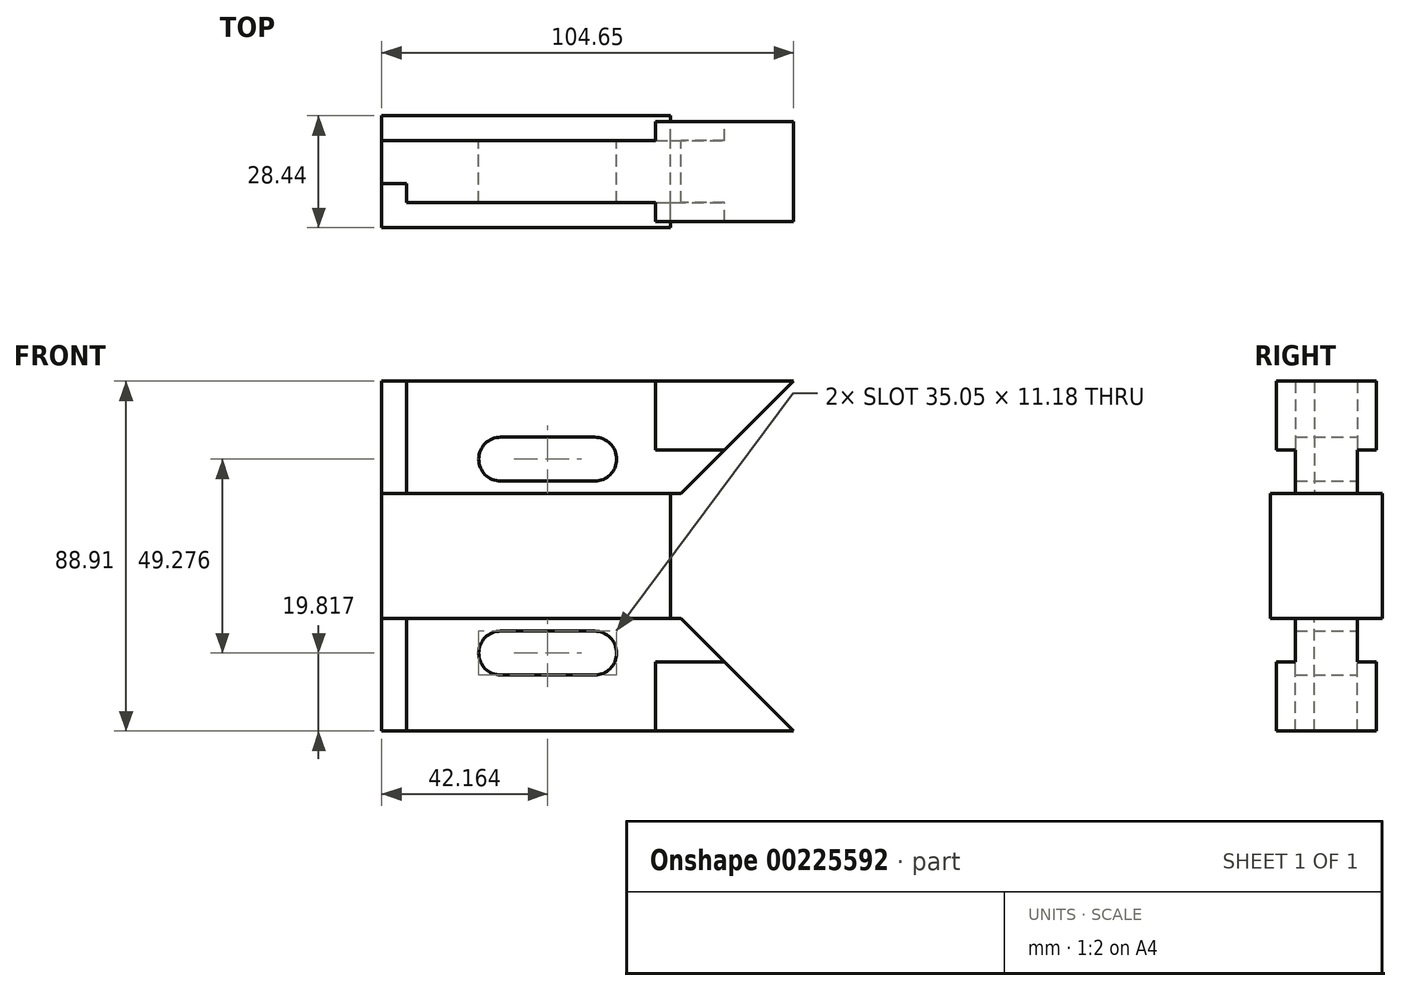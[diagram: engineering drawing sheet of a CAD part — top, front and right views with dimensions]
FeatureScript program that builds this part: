
annotation { "Feature Type Name" : "Feature", "Feature Type Description" : "" }
export const myFeature = defineFeature(function(context is Context, id is Id, definition is map)
    precondition{}
    {
        {
            var Q0;
            Q0=qCreatedBy(makeId("Front.planeOp"),FACE);
            var sketch = newSketch(context, id + "F0", { "sketchPlane" : qUnion([Q0])});
            skLineSegment(sketch, "E0", {"start": v(0, 28.57) * mm, "end": v(0, 0) * mm});
            skLineSegment(sketch, "E1", {"start": v(0, 0) * mm, "end": v(104.65, 0) * mm});
            skLineSegment(sketch, "E2", {"start": v(104.65, 0) * mm, "end": v(104.65, 28.57) * mm});
            skLineSegment(sketch, "E3", {"start": v(104.65, 28.58) * mm, "end": v(0, 28.57) * mm});
            skLineSegment(sketch, "E4", {"start": v(0, 0) * mm, "end": v(0, -15.87) * mm});
            skLineSegment(sketch, "E5", {"start": v(0, -15.88) * mm, "end": v(73.4, -15.88) * mm});
            skLineSegment(sketch, "E6", {"start": v(73.4, -15.88) * mm, "end": v(73.4, 0) * mm});
            skLineSegment(sketch, "E7", {"start": v(104.65, 28.58) * mm, "end": v(76.07, 0) * mm});
            skLineSegment(sketch, "E8", {"start": v(69.6, 28.58) * mm, "end": v(69.6, 11.05) * mm});
            skLineSegment(sketch, "E9", {"start": v(69.6, 11.05) * mm, "end": v(104.65, 11.05) * mm});
            skLineSegment(sketch, "E10", {"start": v(6.35, 28.57) * mm, "end": v(6.35, 0) * mm});
            skCircle(sketch, "E11", {"center": v(30.23, 8.76) * mm, "radius": 5.59 * mm});
            skCircle(sketch, "E12", {"center": v(54.1, 8.76) * mm, "radius": 5.59 * mm});
            skLineSegment(sketch, "E13", {"start": v(30.23, 3.17) * mm, "end": v(30.23, 14.35) * mm});
            skLineSegment(sketch, "E14", {"start": v(30.23, 14.35) * mm, "end": v(54.1, 14.35) * mm});
            skLineSegment(sketch, "E15", {"start": v(54.1, 14.35) * mm, "end": v(54.1, 3.17) * mm});
            skLineSegment(sketch, "E16", {"start": v(54.1, 3.17) * mm, "end": v(30.23, 3.17) * mm});
            skSolve(sketch);
        }
        {
            var Q0;
            {var subQ0=sQuery(id+"F0.wireOp",EDGE,"E4");Q0=makeQuery(id+"F0.imprint","IMPRINT",FACE,{"disambiguationData":[TD([[makeQuery(id+"F0.imprint","IMPRINT",EDGE,{"derivedFrom":subQ0}),1.0]])]});}
            extrude(context, id + "F1", {"entities" : qUnion([Q0]), "endBound" : BoundingType.SYMMETRIC, "depth" : 28.45 * mm});
        }
        {
            var Q0;
            {var subQ3=sQuery(id+"F0.wireOp",EDGE,"E8");Q0=makeQuery(id+"F0.imprint","IMPRINT",FACE,{"disambiguationData":[TD([[makeQuery(id+"F0.imprint","IMPRINT",EDGE,{"derivedFrom":subQ3}),1.0]])]});}
            extrude(context, id + "F2", {"entities" : qUnion([Q0]), "endBound" : BoundingType.SYMMETRIC, "depth" : 25.4 * mm});
        }
        {
            var Q0;
            {var subQ9=sQuery(id+"F0.wireOp",EDGE,"E8");Q0=makeQuery(id+"F0.imprint","IMPRINT",FACE,{"disambiguationData":[TD([[makeQuery(id+"F0.imprint","IMPRINT",EDGE,{"derivedFrom":subQ9}),-1.0]])]});}
            extrude(context, id + "F3", {"entities" : qUnion([Q0]), "endBound" : BoundingType.SYMMETRIC, "depth" : 15.75 * mm});
        }
        {
            var Q0;
            {var subQ0=sQuery(id+"F0.wireOp",EDGE,"E0");Q0=makeQuery(id+"F0.imprint","IMPRINT",FACE,{"disambiguationData":[TD([[makeQuery(id+"F0.imprint","IMPRINT",EDGE,{"derivedFrom":subQ0}),1.0]])]});}
            extrude(context, id + "F4", {"entities" : qUnion([Q0]), "oppositeDirection" : true, "depth" : 7.87 * mm});
        }
        {
            var Q0;
            {var subQ0=sQuery(id+"F0.wireOp",EDGE,"E0");Q0=makeQuery(id+"F0.imprint","IMPRINT",FACE,{"disambiguationData":[TD([[makeQuery(id+"F0.imprint","IMPRINT",EDGE,{"derivedFrom":subQ0}),1.0]])]});}
            extrude(context, id + "F5", {"entities" : qUnion([Q0]), "depth" : 3.05 * mm});
        }
        {
            var Q0;
            Q0=makeQuery(id+"F1.opExtrude","SWEPT_BODY",BODY,{"disambiguationData":[OSD([sQuery(id+"F0.wireOp",EDGE,"E1"),sQuery(id+"F0.wireOp",EDGE,"E4"),sQuery(id+"F0.wireOp",EDGE,"E5"),sQuery(id+"F0.wireOp",EDGE,"E6")])]});
            var Q1;
            Q1=makeQuery(id+"F5.opExtrude","SWEPT_BODY",BODY,{"disambiguationData":[OSD([sQuery(id+"F0.wireOp",EDGE,"E0"),sQuery(id+"F0.wireOp",EDGE,"E1"),sQuery(id+"F0.wireOp",EDGE,"E3"),sQuery(id+"F0.wireOp",EDGE,"E10")])]});
            var Q2;
            Q2=makeQuery(id+"F3.opExtrude","SWEPT_BODY",BODY,{"disambiguationData":[OSD([sQuery(id+"F0.wireOp",EDGE,"E1"),sQuery(id+"F0.wireOp",EDGE,"E3"),sQuery(id+"F0.wireOp",EDGE,"E7"),sQuery(id+"F0.wireOp",EDGE,"E8"),sQuery(id+"F0.wireOp",EDGE,"E9"),sQuery(id+"F0.wireOp",EDGE,"E10"),sQuery(id+"F0.wireOp",EDGE,"E11"),sQuery(id+"F0.wireOp",EDGE,"E12"),sQuery(id+"F0.wireOp",EDGE,"E14"),sQuery(id+"F0.wireOp",EDGE,"E16")])]});
            var Q3;
            Q3=makeQuery(id+"F2.opExtrude","SWEPT_BODY",BODY,{"disambiguationData":[OSD([sQuery(id+"F0.wireOp",EDGE,"E3"),sQuery(id+"F0.wireOp",EDGE,"E7"),sQuery(id+"F0.wireOp",EDGE,"E8"),sQuery(id+"F0.wireOp",EDGE,"E9")])]});
            var Q4;
            Q4=makeQuery(id+"F4.opExtrude","SWEPT_BODY",BODY,{"disambiguationData":[OSD([sQuery(id+"F0.wireOp",EDGE,"E0"),sQuery(id+"F0.wireOp",EDGE,"E1"),sQuery(id+"F0.wireOp",EDGE,"E3"),sQuery(id+"F0.wireOp",EDGE,"E10")])]});
            var Q5;
            Q5=makeQuery(id+"F1.opExtrude","SWEPT_FACE",FACE,{"disambiguationData":[OSD([sQuery(id+"F0.wireOp",EDGE,"E5")])]});
            mirror(context, id + "F6", {"operationType" : NewBodyOperationType.ADD, "entities" : qUnion([Q0, Q1, Q2, Q3, Q4]), "mirrorPlane" : qUnion([Q5])});
        }
    });
